FCSTD DOCUMENT  (FreeCAD 0.20R29410 (Git))
Label: ASM_Base
License: All rights reserved
LicenseURL: http://en.wikipedia.org/wiki/All_rights_reserved
objects: App::Link×5, App::DocumentObjectGroup×3, PartDesign::CoordinateSystem×2, App::FeaturePython×1, App::Part×1
note: 2 computed .brp shape members not serialized (recipe doc carries the construction recipe); baked Part::Feature solids carry a one-line shape summary decoded from their .brp
EXTERNAL_REF file=MainWheel.FCStd obj=LCS_1
EXTERNAL_REF file=MainWheel.FCStd obj=Body
EXTERNAL_REF file=PipeFloorFlange.FCStd obj=LCS_1
EXTERNAL_REF file=PipeFloorFlange.FCStd obj=Body
EXTERNAL_REF file=PipeNipple.FCStd obj=LCS_root
EXTERNAL_REF file=PipeNipple.FCStd obj=Body
EXTERNAL_REF file=PillowBlock.FCStd obj=LCS_0
EXTERNAL_REF file=PipeNipple.FCStd obj=LCS_end
EXTERNAL_REF file=PillowBlock.FCStd obj=Body
EXTERNAL_REF file=SlipRing.FCStd obj=LCS_Origin
EXTERNAL_REF file=SlipRing.FCStd obj=Assembly

FEATURE [App::DocumentObjectGroup] Parts
FEATURE [PartDesign::CoordinateSystem] LCS_Origin
  AttacherType = Attacher::AttachEngine3D
  MapMode = 2
  Support = -> [X_Axis]
FEATURE [App::FeaturePython] Variables  # WARN: FeaturePython — macro-defined, semantics opaque (R4)
  Type = App::PropertyContainer
FEATURE [App::DocumentObjectGroup] Constraints
FEATURE [App::DocumentObjectGroup] Configurations
FEATURE [App::Link] MainWheel
  AssemblyType = Part::Link
  AttachedBy = #LCS_1
  AttachedTo = Parent Assembly#LCS_Origin
  LinkedObject = -> <external MainWheel.FCStd>#Body
  SolverId = Asm4EE
  expr: Placement = LCS_Origin.Placement * AttachmentOffset * MainWheel#LCS_1.Placement ^ -1
FEATURE [App::Link] PipeFlange
  AssemblyType = Part::Link
  AttachedBy = #LCS_1
  AttachedTo = MainWheel#LCS_1
  AttachmentOffset = pos=(0,0,0) rot=(1,0,0;3.14159rad)
  LinkPlacement = pos=(0,0,0) rot=(1,0,0;3.14159rad)
  LinkedObject = -> <external PipeFloorFlange.FCStd>#Body
  Placement = pos=(0,0,0) rot=(1,0,0;3.14159rad)
  SolverId = Asm4EE
  expr: Placement = MainWheel.Placement * MainWheel#LCS_1.Placement * AttachmentOffset * PipeFloorFlange#LCS_1.Placement ^ -1
FEATURE [App::Link] PipeNipple
  AssemblyType = Part::Link
  AttachedBy = #LCS_root
  AttachedTo = PipeFlange#LCS_1
  LinkPlacement = pos=(0,0,0) rot=(1,0,0;3.14159rad)
  LinkedObject = -> <external PipeNipple.FCStd>#Body
  Placement = pos=(0,0,0) rot=(1,0,0;3.14159rad)
  SolverId = Asm4EE
  expr: Placement = PipeFlange.Placement * PipeFloorFlange#LCS_1.Placement * AttachmentOffset * PipeNipple#LCS_root.Placement ^ -1
FEATURE [App::Link] PillowBlock
  AssemblyType = Part::Link
  AttachedBy = #LCS_0
  AttachedTo = PipeNipple#LCS_end
  AttachmentOffset = pos=(0,0,-8) rot=(1,0,0;3.14159rad)
  LinkPlacement = pos=(0,-1.3e-14,-106.3) rot=(0,0,1;0rad)
  LinkedObject = -> <external PillowBlock.FCStd>#Body
  Placement = pos=(0,-1.3e-14,-106.3) rot=(0,0,1;0rad)
  SolverId = Asm4EE
  expr: Placement = PipeNipple.Placement * PipeNipple#LCS_end.Placement * AttachmentOffset * PillowBlock#LCS_0.Placement ^ -1
FEATURE [PartDesign::CoordinateSystem] PillowBlock_LCS_0
  AttachedBy = Origin
  AttacherType = Attacher::AttachEngine3D
  Placement = pos=(0,-1.3e-14,-106.3) rot=(0,0,1;0rad)
  SolverId = Asm4EE
  expr: Placement = PillowBlock.Placement * PillowBlock#LCS_0.Placement
FEATURE [App::Link] SlipRing
  AttachedBy = #LCS_Origin
  AttachedTo = PipeNipple#LCS_end
  AttachmentOffset = pos=(0,0,0) rot=(1,0,0;3.14159rad)
  LinkPlacement = pos=(0,-1.4e-14,-114.3) rot=(0,0,1;0rad)
  LinkedObject = -> <external SlipRing.FCStd>#Assembly
  Placement = pos=(0,-1.4e-14,-114.3) rot=(0,0,1;0rad)
  SolverId = Asm4EE
  expr: Placement = PipeNipple.Placement * PipeNipple#LCS_end.Placement * AttachmentOffset * SlipRing#LCS_Origin.Placement ^ -1
FEATURE [App::Part] Assembly
  AssemblyType = Part::Link
  Group = -> [LCS_Origin,Variables,Constraints,Configurations,MainWheel,PipeFlange,PipeNipple,PillowBlock,PillowBlock_LCS_0,SlipRing]
  Origin = -> Origin
  Type = Assembly

RESOLVED EXTERNAL PARTS (link-assembly join: the EXTERNAL_REF files above that resolve inside this repo's crawl, each included once):
---- part MainWheel.FCStd = doc fcstd_f12e939c456b ----
FCSTD DOCUMENT  (FreeCAD 0.20R29410 (Git))
Label: MainWheel
License: All rights reserved
LicenseURL: http://en.wikipedia.org/wiki/All_rights_reserved
objects: Sketcher::SketchObject×1, PartDesign::CoordinateSystem×1, PartDesign::Pad×1, PartDesign::Body×1
note: 5 computed .brp shape members not serialized (recipe doc carries the construction recipe); baked Part::Feature solids carry a one-line shape summary decoded from their .brp
EXTERNAL_REF file=Params.FCStd obj=Spreadsheet

FEATURE [Sketcher::SketchObject] Sketch001
  FullyConstrained = true
  MapMode = 5
  Support = -> [XY_Plane]
  sketch-geometry (2):
    g0: Circle CenterX=0 CenterY=0 CenterZ=0 NormalX=0 NormalY=0 NormalZ=1 AngleXU=0 Radius=19.05
    g1: Circle CenterX=0 CenterY=0 CenterZ=0 NormalX=0 NormalY=0 NormalZ=1 AngleXU=0 Radius=300
  constraints (4):
    c: Coincident(g0,g-1)
    c: Diameter(g0) = 38.1
    c: Coincident(g1,g0)
    c: Diameter(g1) = 600
FEATURE [PartDesign::CoordinateSystem] LCS_1
  AttacherType = Attacher::AttachEngine3D
  MapMode = 2
  Support = -> [XY_Plane]
FEATURE [PartDesign::Pad] Pad
  Direction = (0,0,1)
  Length = 18.5
  Length2 = 10
  Profile = -> Sketch001
  ReferenceAxis = -> Sketch001 [N_Axis]
  Type = 0
  expr: Length = <<Params>>#<<Params>>.PlywoodThickness
FEATURE [PartDesign::Body] Body
  Group = -> [Sketch001,LCS_1,Pad]
  Origin = -> Origin
  Tip = -> Pad
---- part PillowBlock.FCStd = doc fcstd_dc4ef761c73f ----
FCSTD DOCUMENT  (FreeCAD 0.20R29410 (Git))
Label: PillowBlock
License: All rights reserved
LicenseURL: http://en.wikipedia.org/wiki/All_rights_reserved
objects: Sketcher::SketchObject×2, PartDesign::CoordinateSystem×1, PartDesign::Revolution×1, PartDesign::Pad×1, PartDesign::Body×1
note: 8 computed .brp shape members not serialized (recipe doc carries the construction recipe); baked Part::Feature solids carry a one-line shape summary decoded from their .brp

FEATURE [PartDesign::CoordinateSystem] LCS_0
  AttacherType = Attacher::AttachEngine3D
  MapMode = 2
  Support = -> [X_Axis]
FEATURE [Sketcher::SketchObject] Sketch
  FullyConstrained = true
  MapMode = 5
  Placement = pos=(0,0,0) rot=(1,0,0;1.5708rad)
  Support = -> [XZ_Plane]
  sketch-geometry (6):
    g0: LineSegment StartX=19.05 StartY=0 StartZ=0 EndX=19.05 EndY=51.2064 EndZ=0
    g1: LineSegment StartX=43.4 StartY=36.068 StartZ=0 EndX=51.05 EndY=0 EndZ=0
    g2: LineSegment StartX=51.05 StartY=0 StartZ=0 EndX=19.05 EndY=0 EndZ=0
    g3: LineSegment StartX=43.4 StartY=36.068 StartZ=0 EndX=25.4 EndY=36.068 EndZ=0
    g4: LineSegment StartX=25.4 StartY=36.068 StartZ=0 EndX=25.4 EndY=51.2064 EndZ=0
    g5: LineSegment StartX=25.4 StartY=51.2064 StartZ=0 EndX=19.05 EndY=51.2064 EndZ=0
  constraints (18):
    c: PointOnObject(g0,g-1)
    c: Vertical(g0)
    c: PointOnObject(g2,g-1)
    c: Coincident(g2,g0)
    c: Coincident(g1,g2)
    c: DistanceX(g-1,g0) = 19.05  'ShaftRadius'
    c: Coincident(g1,g3)
    c: Horizontal(g3)
    c: Coincident(g3,g4)
    c: Vertical(g4)
    c: Coincident(g4,g5)
    c: Horizontal(g5)
    c: Coincident(g5,g0)
    c: DistanceY(g1,g1) = 36.068
    c: DistanceY(g1,g4) = 51.2064
    c: DistanceX(g5,g5) = 6.35
    c: DistanceX(g3,g3) = 18
    c: DistanceX(g2,g2) = 32
FEATURE [PartDesign::Revolution] Revolution
  Angle = 360
  Axis = (0,-2e-16,1)
  Base = (0,0,0)
  Placement = pos=(0,0,0) rot=(1,0,0;1.5708rad)
  Profile = -> Sketch
  ReferenceAxis = -> Sketch [V_Axis]
  Reversed = true
FEATURE [Sketcher::SketchObject] Sketch001
  FullyConstrained = true
  MapMode = 5
  Support = -> [XY_Plane]
  expr: Constraints[32] = <<Sketch>>.Constraints.ShaftRadius
  sketch-geometry (15):
    g0: ArcOfCircle CenterX=-51.0032 CenterY=51.0032 CenterZ=0 NormalX=0 NormalY=0 NormalZ=1 AngleXU=0 Radius=14.0843 StartAngle=1.5708 EndAngle=3.14159
    g1: LineSegment StartX=-51.0032 StartY=65.0875 StartZ=0 EndX=51.0032 EndY=65.0875 EndZ=0
    g2: ArcOfCircle CenterX=51.0032 CenterY=51.0032 CenterZ=0 NormalX=0 NormalY=0 NormalZ=1 AngleXU=0 Radius=14.0843 StartAngle=3e-16 EndAngle=1.5708
    g3: LineSegment StartX=65.0875 StartY=51.0032 StartZ=0 EndX=65.0875 EndY=-51.0032 EndZ=0
    g4: ArcOfCircle CenterX=51.0032 CenterY=-51.0032 CenterZ=0 NormalX=0 NormalY=0 NormalZ=1 AngleXU=0 Radius=14.0843 StartAngle=4.71239 EndAngle=6.28319
    g5: LineSegment StartX=51.0032 StartY=-65.0875 StartZ=0 EndX=-51.0032 EndY=-65.0875 EndZ=0
    g6: ArcOfCircle CenterX=-51.0032 CenterY=-51.0032 CenterZ=0 NormalX=0 NormalY=0 NormalZ=1 AngleXU=0 Radius=14.0843 StartAngle=3.14159 EndAngle=4.71239
    g7: LineSegment StartX=-65.0875 StartY=-51.0032 StartZ=0 EndX=-65.0875 EndY=51.0032 EndZ=0
    g8: GeomPoint X=-65.0875 Y=65.0875 Z=0
    g9: GeomPoint X=65.0875 Y=-65.0875 Z=0
    g10: Circle CenterX=51.0032 CenterY=51.0032 CenterZ=0 NormalX=0 NormalY=0 NormalZ=1 AngleXU=0 Radius=7
    g11: Circle CenterX=-51.0032 CenterY=51.0032 CenterZ=0 NormalX=0 NormalY=0 NormalZ=1 AngleXU=0 Radius=7
    g12: Circle CenterX=-51.0032 CenterY=-51.0032 CenterZ=0 NormalX=0 NormalY=0 NormalZ=1 AngleXU=0 Radius=7
    g13: Circle CenterX=51.0032 CenterY=-51.0032 CenterZ=0 NormalX=0 NormalY=0 NormalZ=1 AngleXU=0 Radius=7
    g14: Circle CenterX=0 CenterY=0 CenterZ=0 NormalX=0 NormalY=0 NormalZ=1 AngleXU=0 Radius=19.05
  constraints (33):
    c: Tangent(g0,g1) = 1.5708
    c: Tangent(g1,g2) = 1.5708
    c: Tangent(g2,g3) = 1.5708
    c: Tangent(g3,g4) = 1.5708
    c: Tangent(g4,g5) = 1.5708
    c: Tangent(g5,g6) = 1.5708
    c: Tangent(g6,g7) = 1.5708
    c: Tangent(g7,g0) = 1.5708
    c: Horizontal(g1)
    c: Horizontal(g5)
    c: Vertical(g3)
    c: Vertical(g7)
    c: Equal(g0,g2)
    c: Equal(g2,g4)
    c: Equal(g4,g6)
    c: PointOnObject(g8,g1)
    c: PointOnObject(g8,g7)
    c: PointOnObject(g9,g3)
    c: PointOnObject(g9,g5)
    c: Equal(g1,g3)
    c: Symmetric(g2,g6,g-1)
    c: DistanceY(g4,g2) = 102.006
    c: Coincident(g10,g2)
    c: Coincident(g11,g0)
    c: Coincident(g12,g6)
    c: Coincident(g13,g4)
    c: Equal(g13,g12)
    c: Equal(g12,g11)
    c: Equal(g11,g10)
    c: Diameter(g10) = 14
    c: DistanceY(g4,g1) = 130.175
    c: Coincident(g14,g-1)
    c: Radius(g14) = 19.05
FEATURE [PartDesign::Pad] Pad
  BaseFeature = -> Revolution
  Direction = (0,0,1)
  Length = 15.875
  Length2 = 10
  Placement = pos=(0,0,0) rot=(1,0,0;1.5708rad)
  Profile = -> Sketch001
  ReferenceAxis = -> Sketch001 [N_Axis]
  Type = 0
FEATURE [PartDesign::Body] Body
  Group = -> [LCS_0,Sketch,Revolution,Sketch001,Pad]
  Origin = -> Origin
  Tip = -> Pad
---- part PipeFloorFlange.FCStd = doc fcstd_4d18ebb2da03 ----
FCSTD DOCUMENT  (FreeCAD 0.20R29410 (Git))
Label: PipeFloorFlange
License: All rights reserved
LicenseURL: http://en.wikipedia.org/wiki/All_rights_reserved
objects: Sketcher::SketchObject×2, PartDesign::Revolution×1, PartDesign::Hole×1, PartDesign::PolarPattern×1, PartDesign::CoordinateSystem×1, PartDesign::Body×1
note: 9 computed .brp shape members not serialized (recipe doc carries the construction recipe); baked Part::Feature solids carry a one-line shape summary decoded from their .brp

FEATURE [Sketcher::SketchObject] Sketch
  FullyConstrained = true
  MapMode = 5
  Placement = pos=(0,0,0) rot=(1,0,0;1.5708rad)
  Support = -> [XZ_Plane]
  sketch-geometry (6):
    g0: LineSegment StartX=14.86 StartY=0 StartZ=0 EndX=47.625 EndY=0 EndZ=0
    g1: LineSegment StartX=47.625 StartY=0 StartZ=0 EndX=47.625 EndY=8 EndZ=0
    g2: LineSegment StartX=47.625 StartY=8 StartZ=0 EndX=22.86 EndY=8 EndZ=0
    g3: LineSegment StartX=22.86 StartY=8 StartZ=0 EndX=22.86 EndY=17.78 EndZ=0
    g4: LineSegment StartX=22.86 StartY=17.78 StartZ=0 EndX=14.86 EndY=17.78 EndZ=0
    g5: LineSegment StartX=14.86 StartY=17.78 StartZ=0 EndX=14.86 EndY=0 EndZ=0
  constraints (18):
    c: PointOnObject(g0,g-1)
    c: Horizontal(g0)
    c: Coincident(g1,g0)
    c: Coincident(g2,g1)
    c: Horizontal(g2)
    c: Coincident(g3,g2)
    c: Vertical(g3)
    c: Coincident(g4,g3)
    c: Horizontal(g4)
    c: Vertical(g5)
    c: Coincident(g5,g4)
    c: Coincident(g5,g0)
    c: Vertical(g1)
    c: DistanceX(g-1,g3) = 22.86
    c: DistanceY(g1,g1) = 8  'Thickness'
    c: DistanceY(g5,g5) = 17.78
    c: DistanceX(g-1,g0) = 47.625
    c: DistanceX(g4,g4) = 8
FEATURE [PartDesign::Revolution] Revolution
  Angle = 360
  Axis = (0,-2e-16,1)
  Base = (0,0,0)
  Placement = pos=(0,0,0) rot=(1,0,0;1.5708rad)
  Profile = -> Sketch
  ReferenceAxis = -> Sketch [V_Axis]
  Reversed = true
FEATURE [Sketcher::SketchObject] Sketch001
  AttachmentOffset = pos=(0,0,8) rot=(0,0,1;0rad)
  FullyConstrained = true
  MapMode = 5
  Placement = pos=(0,0,8) rot=(0,0,1;0rad)
  Support = -> [XY_Plane]
  expr: .AttachmentOffset.Base.z = <<Sketch>>.Constraints.Thickness
  sketch-geometry (1):
    g0: Circle CenterX=0 CenterY=35 CenterZ=0 NormalX=0 NormalY=0 NormalZ=1 AngleXU=0 Radius=3
  constraints (3):
    c: PointOnObject(g0,g-2)
    c: DistanceY(g-1,g0) = 35
    c: Diameter(g0) = 6
FEATURE [PartDesign::Hole] Hole
  BaseFeature = -> Revolution
  CustomThreadClearance = 0
  Depth = 25
  DepthType = 0
  Diameter = 8.7
  DrillForDepth = false
  DrillPoint = 1
  DrillPointAngle = 118
  HoleCutCountersinkAngle = 82
  HoleCutCustomValues = false
  HoleCutDepth = 0
  HoleCutDiameter = 14.79
  HoleCutType = 2
  ModelThread = false
  Placement = pos=(0,0,0) rot=(1,0,0;1.5708rad)
  Profile = -> Sketch001
  Tapered = false
  TaperedAngle = 90
  ThreadClass = 0
  ThreadDepth = 25
  ThreadDepthType = 0
  ThreadDirection = 0
  ThreadFit = 0
  ThreadSize = 10
  ThreadType = 3
  Threaded = false
  UseCustomThreadClearance = false
FEATURE [PartDesign::PolarPattern] PolarPattern
  Angle = 360
  Axis = -> Sketch001 [N_Axis]
  BaseFeature = -> Hole
  Occurrences = 4
  Originals = -> [Hole]
  Placement = pos=(0,0,0) rot=(1,0,0;1.5708rad)
FEATURE [PartDesign::CoordinateSystem] LCS_1
  AttacherType = Attacher::AttachEngine3D
  MapMode = 2
  Support = -> [XY_Plane]
FEATURE [PartDesign::Body] Body
  Group = -> [Sketch,Revolution,Sketch001,Hole,PolarPattern,LCS_1]
  Origin = -> Origin
  Tip = -> PolarPattern
---- part PipeNipple.FCStd = doc fcstd_909803d2c7c9 ----
FCSTD DOCUMENT  (FreeCAD 0.20R29410 (Git))
Label: PipeNipple
License: All rights reserved
LicenseURL: http://en.wikipedia.org/wiki/All_rights_reserved
objects: PartDesign::CoordinateSystem×2, Sketcher::SketchObject×1, PartDesign::Pad×1, PartDesign::Body×1
note: 6 computed .brp shape members not serialized (recipe doc carries the construction recipe); baked Part::Feature solids carry a one-line shape summary decoded from their .brp

FEATURE [Sketcher::SketchObject] Sketch
  FullyConstrained = true
  MapMode = 5
  Support = -> [XY_Plane]
  sketch-geometry (2):
    g0: Circle CenterX=0 CenterY=0 CenterZ=0 NormalX=0 NormalY=0 NormalZ=1 AngleXU=0 Radius=13.3223
    g1: Circle CenterX=0 CenterY=0 CenterZ=0 NormalX=0 NormalY=0 NormalZ=1 AngleXU=0 Radius=16.7005
  constraints (4):
    c: Coincident(g0,g-1)
    c: Coincident(g1,g0)
    c: Diameter(g1) = 33.401
    c: Diameter(g0) = 26.6446
FEATURE [PartDesign::Pad] Pad
  Direction = (0,0,1)
  Length = 114.3
  Length2 = 10
  Profile = -> Sketch
  ReferenceAxis = -> Sketch [N_Axis]
  Type = 0
FEATURE [PartDesign::CoordinateSystem] LCS_root
  AttacherType = Attacher::AttachEngine3D
  MapMode = 2
  Support = -> [XY_Plane]
FEATURE [PartDesign::CoordinateSystem] LCS_end
  AttacherType = Attacher::AttachEngine3D
  AttachmentOffset = pos=(0,0,114.3) rot=(0,0,1;0rad)
  MapMode = 2
  Placement = pos=(0,0,114.3) rot=(0,0,1;0rad)
  Support = -> [LCS_root]
  expr: .AttachmentOffset.Base.z = <<Pad>>.Length
FEATURE [PartDesign::Body] Body
  Group = -> [Sketch,Pad,LCS_root,LCS_end]
  Origin = -> Origin
  Tip = -> Pad
---- part SlipRing.FCStd = doc fcstd_41cefa76d6a6 ----
FCSTD DOCUMENT  (FreeCAD 0.20R29410 (Git))
Label: SlipRing
License: All rights reserved
LicenseURL: http://en.wikipedia.org/wiki/All_rights_reserved
objects: App::DocumentObjectGroup×3, PartDesign::CoordinateSystem×1, App::FeaturePython×1, Sketcher::SketchObject×1, PartDesign::Revolution×1, PartDesign::Body×1, App::Part×1
note: 5 computed .brp shape members not serialized (recipe doc carries the construction recipe); baked Part::Feature solids carry a one-line shape summary decoded from their .brp

FEATURE [App::DocumentObjectGroup] Parts
FEATURE [PartDesign::CoordinateSystem] LCS_Origin
  AttacherType = Attacher::AttachEngine3D
  MapMode = 2
  Support = -> [X_Axis]
FEATURE [App::FeaturePython] Variables  # WARN: FeaturePython — macro-defined, semantics opaque (R4)
  Type = App::PropertyContainer
FEATURE [App::DocumentObjectGroup] Constraints
FEATURE [App::DocumentObjectGroup] Configurations
FEATURE [Sketcher::SketchObject] Sketch
  FullyConstrained = true
  MapMode = 5
  Placement = pos=(0,0,0) rot=(1,0,0;1.5708rad)
  Support = -> [XZ_Plane001]
  sketch-geometry (14):
    g0: LineSegment StartX=0 StartY=38.6 StartZ=0 EndX=11 EndY=38.6 EndZ=0
    g1: LineSegment StartX=11 StartY=38.6 StartZ=0 EndX=11 EndY=0 EndZ=0
    g2: LineSegment StartX=11 StartY=0 StartZ=0 EndX=22.2 EndY=0 EndZ=0
    g3: LineSegment StartX=22.2 StartY=0 StartZ=0 EndX=22.2 EndY=-2.6 EndZ=0
    g4: LineSegment StartX=22.2 StartY=-2.6 StartZ=0 EndX=11 EndY=-2.6 EndZ=0
    g5: LineSegment StartX=11 StartY=-2.6 StartZ=0 EndX=11 EndY=-8.6 EndZ=0
    g6: LineSegment StartX=11 StartY=-8.6 StartZ=0 EndX=5 EndY=-8.6 EndZ=0
    g7: LineSegment StartX=5 StartY=-8.6 StartZ=0 EndX=5 EndY=-14.6 EndZ=0
    g8: LineSegment StartX=0 StartY=-14.6 StartZ=0 EndX=0 EndY=38.6 EndZ=0
    g9: LineSegment StartX=5 StartY=-14.6 StartZ=0 EndX=4 EndY=-14.6 EndZ=0
    g10: LineSegment StartX=4 StartY=-14.6 StartZ=0 EndX=0 EndY=-14.6 EndZ=0
    g11: LineSegment StartX=4 StartY=-14.6 StartZ=0 EndX=4 EndY=-30.6 EndZ=0
    g12: LineSegment StartX=4 StartY=-30.6 StartZ=0 EndX=0 EndY=-30.6 EndZ=0
    g13: LineSegment StartX=0 StartY=-30.6 StartZ=0 EndX=0 EndY=-14.6 EndZ=0
  constraints (41):
    c: PointOnObject(g0,g-2)
    c: Horizontal(g0)
    c: Coincident(g0,g1)
    c: Vertical(g1)
    c: Coincident(g1,g2)
    c: Horizontal(g2)
    c: Coincident(g2,g3)
    c: Vertical(g3)
    c: Coincident(g3,g4)
    c: Horizontal(g4)
    c: Coincident(g4,g5)
    c: Vertical(g5)
    c: Coincident(g5,g6)
    c: Coincident(g6,g7)
    c: Vertical(g7)
    c: Coincident(g7,g9)
    c: PointOnObject(g10,g-2)
    c: Coincident(g10,g8)
    c: Coincident(g8,g0)
    c: Horizontal(g6)
    c: DistanceX(g0,g0) = 11
    c: DistanceX(g-1,g3) = 22.2
    c: PointOnObject(g1,g5)
    c: DistanceX(g10,g9) = 5
    c: DistanceY(g7,g7) = 6
    c: DistanceY(g5,g5) = 6
    c: DistanceY(g3,g3) = 2.6
    c: DistanceY(g1,g1) = 38.6
    c: PointOnObject(g1,g-1)
    c: Coincident(g9,g10)
    c: Horizontal(g9)
    c: Horizontal(g10)
    c: Coincident(g11,g9)
    c: Vertical(g11)
    c: Coincident(g12,g11)
    c: PointOnObject(g12,g-2)
    c: Horizontal(g12)
    c: Coincident(g13,g12)
    c: Coincident(g13,g8)
    c: DistanceX(g12,g12) = 4
    c: DistanceY(g13,g13) = 16
FEATURE [PartDesign::Revolution] Revolution
  Angle = 360
  Axis = (0,-2e-16,1)
  Base = (0,0,0)
  Placement = pos=(0,0,0) rot=(1,0,0;1.5708rad)
  Profile = -> Sketch
  ReferenceAxis = -> Sketch [V_Axis]
  Reversed = true
FEATURE [PartDesign::Body] Body
  Group = -> [Sketch,Revolution]
  Origin = -> Origin001
  Tip = -> Revolution
FEATURE [App::Part] Assembly
  AssemblyType = Part::Link
  Group = -> [LCS_Origin,Variables,Constraints,Configurations,Body]
  Origin = -> Origin
  Type = Assembly
